# Revit family: FantiniCosmi_BIM_CH115-16
name_source: partatom
category: Modelli generici
units: mm (PartAtom-declared; Revit-internal decimal feet)

## family parameters
Basato su piano di lavoro = No
Condiviso = No
Punto di calcolo locali = No
Può ospitare armatura = No
Quota connettore circolare = Usa diametro
Sempre verticale = Sì
Taglio con vuoti quando caricato = No
Tipo di parte = Normale

## types (1)
- Standard
    Body admissible temperature = - 10 ÷ 50 °C
    Catalog web link = https://www.fantinicosmi.it
    Color = White
    Descrizione = Electronic room thermostat with batteries, 3 temperature levels
    Differential = 0,5 K
    Maximum ambient temperature = 45 °C
    Micro disconnection = 1B
    Part Number = CH115-16
    Power supply = 2 batteries AA
    Prospetto di default = 0 mm  [stored 0 ft]
    Protection degree = IP20
    Temperature regulation range = 2 ÷ 40 °C

note: [stored X ft] marks values corroborated as IEEE doubles in the binary element streams (Revit-internal decimal feet)

## geometry (parser evidence)
native form markers: Sweep x3
no freeform markers — native parametric forms only
